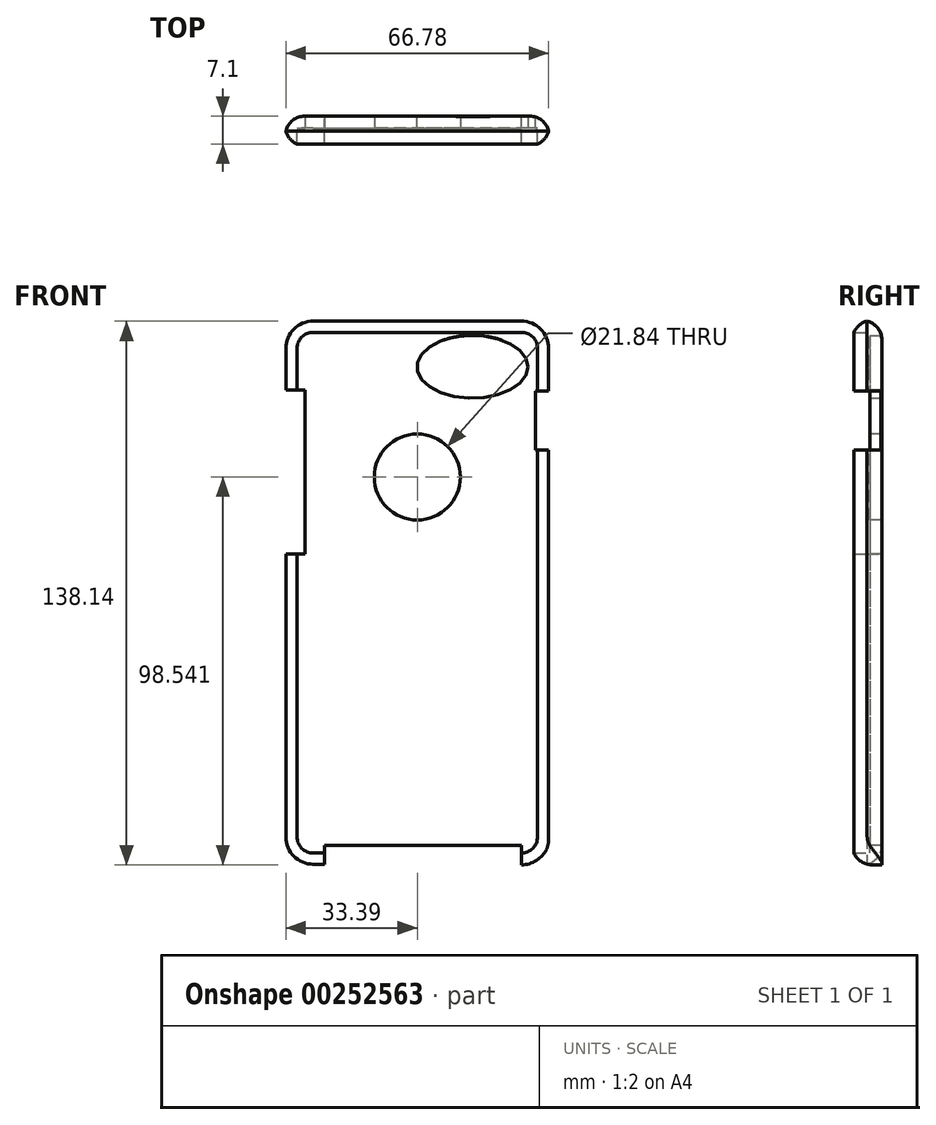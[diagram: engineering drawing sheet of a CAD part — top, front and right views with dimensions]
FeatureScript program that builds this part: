
annotation { "Feature Type Name" : "Feature", "Feature Type Description" : "" }
export const myFeature = defineFeature(function(context is Context, id is Id, definition is map)
    precondition{}
    {
        {
            var Q0;
            Q0=qCreatedBy(makeId("Front.planeOp"),FACE);
            var sketch = newSketch(context, id + "F0", { "sketchPlane" : qUnion([Q0])});
            skLineSegment(sketch, "E0.bottom", {"start": v(-33.55, 69.15) * mm, "end": v(33.55, 69.15) * mm});
            skLineSegment(sketch, "E0.top", {"start": v(-33.55, -69.15) * mm, "end": v(33.55, -69.15) * mm});
            skLineSegment(sketch, "E0.left", {"start": v(-33.55, 69.15) * mm, "end": v(-33.55, -69.15) * mm});
            skLineSegment(sketch, "E0.right", {"start": v(33.55, 69.15) * mm, "end": v(33.55, -69.15) * mm});
            skPoint(sketch, "E0.middle", {"position": v(0, 0) * mm});
            skSolve(sketch);
        }
        {
            var Q0;
            Q0=makeQuery(id+"F0.imprint","IMPRINT",FACE,{"disambiguationData":[TD([[makeQuery(id+"F0.imprint","IMPRINT",EDGE,{"derivedFrom":sQuery(id+"F0.wireOp",EDGE,"E0.bottom")}),-1.0]])]});
            extrude(context, id + "F1", {"entities" : qUnion([Q0]), "depth" : 7.1 * mm});
        }
        {
            var Q0;
            Q0=makeQuery(id+"F1.opExtrude","SWEPT_EDGE",EDGE,{"disambiguationData":[OSD([sQuery(id+"F0.wireOp",EDGE,"E0.bottom"),sQuery(id+"F0.wireOp",EDGE,"E0.right")])]});
            var Q1;
            Q1=makeQuery(id+"F1.opExtrude","SWEPT_EDGE",EDGE,{"disambiguationData":[OSD([sQuery(id+"F0.wireOp",EDGE,"E0.top"),sQuery(id+"F0.wireOp",EDGE,"E0.left")])]});
            var Q2;
            Q2=makeQuery(id+"F1.opExtrude","SWEPT_EDGE",EDGE,{"disambiguationData":[OSD([sQuery(id+"F0.wireOp",EDGE,"E0.top"),sQuery(id+"F0.wireOp",EDGE,"E0.right")])]});
            var Q3;
            Q3=makeQuery(id+"F1.opExtrude","SWEPT_EDGE",EDGE,{"disambiguationData":[OSD([sQuery(id+"F0.wireOp",EDGE,"E0.bottom"),sQuery(id+"F0.wireOp",EDGE,"E0.left")])]});
            fillet(context, id + "F2", {"entities" : qUnion([Q0, Q1, Q2, Q3]), "radius" : 7.1 * mm, "tangentPropagation" : true, "allowEdgeOverflow" : false});
        }
        {
            var Q0;
            Q0=makeQuery(id+"F1.opExtrude","CAP_FACE",FACE,{"disambiguationData":[OSD([sQuery(id+"F0.wireOp",EDGE,"E0.bottom"),sQuery(id+"F0.wireOp",EDGE,"E0.top"),sQuery(id+"F0.wireOp",EDGE,"E0.left"),sQuery(id+"F0.wireOp",EDGE,"E0.right")])],"isStart":false});
            shell(context, id + "F3", {"entities" : qUnion([Q0]), "thickness" : 3 * mm});
        }
        {
            var Q0;
            Q0=makeQuery(id+"F3.opShell","OFFSET_FACE",FACE,{"disambiguationData":[OSD([sQuery(id+"F0.wireOp",EDGE,"E0.bottom"),sQuery(id+"F0.wireOp",EDGE,"E0.top"),sQuery(id+"F0.wireOp",EDGE,"E0.left"),sQuery(id+"F0.wireOp",EDGE,"E0.right")])]});
            var sketch = newSketch(context, id + "F4", { "sketchPlane" : qUnion([Q0])});
            skEllipse(sketch, "E1", {"center": v(14.06, 57.39) * mm, "majorRadius": 14.1 * mm, "minorRadius": 7.98 * mm, "majorAxis": v(1, 0)});
            skCircle(sketch, "E2", {"center": v(0, 29.4) * mm, "radius": 10.92 * mm});
            skSolve(sketch);
        }
        {
            var Q0;
            Q0=makeQuery(id+"F4.imprint","IMPRINT",FACE,{"disambiguationData":[TD([[makeQuery(id+"F4.imprint","IMPRINT",EDGE,{"derivedFrom":sQuery(id+"F4.wireOp",EDGE,"E1")}),1.0]])]});
            var Q1;
            Q1=makeQuery(id+"F4.imprint","IMPRINT",FACE,{"disambiguationData":[TD([[makeQuery(id+"F4.imprint","IMPRINT",EDGE,{"derivedFrom":sQuery(id+"F4.wireOp",EDGE,"E2")}),1.0]])]});
            extrude(context, id + "F5", {"entities" : qUnion([Q0, Q1]), "operationType" : NewBodyOperationType.REMOVE, "endBound" : BoundingType.SYMMETRIC, "oppositeDirection" : true, "depth" : 25 * mm});
        }
        {
            var Q0;
            Q0=makeQuery(id+"F1.opExtrude","SWEPT_FACE",FACE,{"disambiguationData":[OSD([sQuery(id+"F0.wireOp",EDGE,"E0.top")])]});
            var sketch = newSketch(context, id + "F6", { "sketchPlane" : qUnion([Q0])});
            skLineSegment(sketch, "E3.bottom", {"start": v(-23.53, 0) * mm, "end": v(26.45, 0) * mm});
            skLineSegment(sketch, "E3.top", {"start": v(-23.53, 7.1) * mm, "end": v(26.45, 7.1) * mm});
            skLineSegment(sketch, "E3.left", {"start": v(-23.53, 0) * mm, "end": v(-23.53, 7.1) * mm});
            skLineSegment(sketch, "E3.right", {"start": v(26.45, 0) * mm, "end": v(26.45, 7.1) * mm});
            skLineSegment(sketch, "E4.bottom", {"start": v(-23.53, 7.1) * mm, "end": v(-26.45, 7.1) * mm});
            skLineSegment(sketch, "E4.top", {"start": v(-23.53, 7.1) * mm, "end": v(-26.45, 7.1) * mm});
            skLineSegment(sketch, "E4.left", {"start": v(-23.53, 7.1) * mm, "end": v(-23.53, 7.1) * mm});
            skLineSegment(sketch, "E4.right", {"start": v(-26.45, 7.1) * mm, "end": v(-26.45, 7.1) * mm});
            skSolve(sketch);
        }
        {
            var Q0;
            Q0=makeQuery(id+"F6.imprint","IMPRINT",FACE,{"disambiguationData":[TD([[makeQuery(id+"F6.imprint","IMPRINT",EDGE,{"derivedFrom":sQuery(id+"F6.wireOp",EDGE,"E3.bottom")}),1.0]])]});
            extrude(context, id + "F7", {"entities" : qUnion([Q0]), "operationType" : NewBodyOperationType.REMOVE, "endBound" : BoundingType.SYMMETRIC, "oppositeDirection" : true, "depth" : 10 * mm});
        }
        {
            var Q0;
            Q0=makeQuery(id+"F1.opExtrude","SWEPT_FACE",FACE,{"disambiguationData":[OSD([sQuery(id+"F0.wireOp",EDGE,"E0.left")])]});
            var sketch = newSketch(context, id + "F8", { "sketchPlane" : qUnion([Q0])});
            skLineSegment(sketch, "E5.bottom", {"start": v(0, 51.55) * mm, "end": v(7.1, 51.55) * mm});
            skLineSegment(sketch, "E5.top", {"start": v(0, 9.8) * mm, "end": v(7.1, 9.8) * mm});
            skLineSegment(sketch, "E5.left", {"start": v(0, 51.55) * mm, "end": v(0, 9.8) * mm});
            skLineSegment(sketch, "E5.right", {"start": v(7.1, 51.55) * mm, "end": v(7.1, 9.8) * mm});
            skSolve(sketch);
        }
        {
            var Q0;
            Q0=makeQuery(id+"F8.imprint","IMPRINT",FACE,{"disambiguationData":[TD([[makeQuery(id+"F8.imprint","IMPRINT",EDGE,{"derivedFrom":sQuery(id+"F8.wireOp",EDGE,"E5.bottom")}),-1.0]])]});
            extrude(context, id + "F9", {"entities" : qUnion([Q0]), "operationType" : NewBodyOperationType.REMOVE, "endBound" : BoundingType.SYMMETRIC, "oppositeDirection" : true, "depth" : 10 * mm});
        }
        {
            var Q0;
            Q0=makeQuery(id+"F1.opExtrude","SWEPT_FACE",FACE,{"disambiguationData":[OSD([sQuery(id+"F0.wireOp",EDGE,"E0.right")])]});
            var sketch = newSketch(context, id + "F10", { "sketchPlane" : qUnion([Q0])});
            skLineSegment(sketch, "E6.bottom", {"start": v(-7.1, 51.21) * mm, "end": v(0, 51.21) * mm});
            skLineSegment(sketch, "E6.top", {"start": v(-7.1, 36.21) * mm, "end": v(0, 36.21) * mm});
            skLineSegment(sketch, "E6.left", {"start": v(-7.1, 51.21) * mm, "end": v(-7.1, 36.21) * mm});
            skLineSegment(sketch, "E6.right", {"start": v(0, 51.21) * mm, "end": v(0, 36.21) * mm});
            skSolve(sketch);
        }
        {
            var Q0;
            Q0=makeQuery(id+"F10.imprint","IMPRINT",FACE,{"disambiguationData":[TD([[makeQuery(id+"F10.imprint","IMPRINT",EDGE,{"derivedFrom":sQuery(id+"F10.wireOp",EDGE,"E6.bottom")}),-1.0]])]});
            extrude(context, id + "F11", {"entities" : qUnion([Q0]), "operationType" : NewBodyOperationType.REMOVE, "endBound" : BoundingType.SYMMETRIC, "oppositeDirection" : true, "depth" : 7 * mm});
        }
        {
            var Q0;
            {var subQ0=sQuery(id+"F0.wireOp",EDGE,"E0.left");var subQ1=sQuery(id+"F0.wireOp",EDGE,"E0.bottom");Q0=makeQuery(id+"F2.opFillet","BLEND_EDGE",EDGE,{"blendedFrom":[makeQuery(id+"F1.opExtrude","SWEPT_EDGE",EDGE,{"disambiguationData":[OSD([subQ1,subQ0])]}),makeQuery(id+"F1.opExtrude","CAP_FACE",FACE,{"disambiguationData":[OSD([subQ1,sQuery(id+"F0.wireOp",EDGE,"E0.top"),subQ0,sQuery(id+"F0.wireOp",EDGE,"E0.right")])],"isStart":false})],"blendedInto":[makeQuery(id+"F1.opExtrude","CAP_FACE",FACE,{"disambiguationData":[OSD([subQ1,sQuery(id+"F0.wireOp",EDGE,"E0.top"),subQ0,sQuery(id+"F0.wireOp",EDGE,"E0.right")])],"isStart":false})]});}
            var Q1;
            {var subQ0=sQuery(id+"F0.wireOp",EDGE,"E0.left");Q1=makeQuery(id+"F9.boolean.opBoolean","SPLIT",EDGE,{"disambiguationData":[TD([makeQuery(id+"F9.opExtrude","SWEPT_FACE",FACE,{"disambiguationData":[OSD([sQuery(id+"F8.wireOp",EDGE,"E5.bottom")])]})])],"derivedFrom":makeQuery(id+"F1.opExtrude","CAP_EDGE",EDGE,{"disambiguationData":[OSD([subQ0])],"isStart":true})});}
            var Q2;
            Q2=makeQuery(id+"F9.boolean.opBoolean","COPY",EDGE,{"derivedFrom":makeQuery(id+"F9.opExtrude","CAP_EDGE",EDGE,{"disambiguationData":[OSD([sQuery(id+"F8.wireOp",EDGE,"E5.left")])],"isStart":false})});
            var Q3;
            {var subQ0=sQuery(id+"F0.wireOp",EDGE,"E0.left");Q3=makeQuery(id+"F9.boolean.opBoolean","SPLIT",EDGE,{"disambiguationData":[TD([makeQuery(id+"F9.opExtrude","SWEPT_FACE",FACE,{"disambiguationData":[OSD([sQuery(id+"F8.wireOp",EDGE,"E5.top")])]})])],"derivedFrom":makeQuery(id+"F1.opExtrude","CAP_EDGE",EDGE,{"disambiguationData":[OSD([subQ0])],"isStart":true})});}
            var Q4;
            {var subQ0=sQuery(id+"F0.wireOp",EDGE,"E0.left");Q4=makeQuery(id+"F9.boolean.opBoolean","SPLIT",EDGE,{"disambiguationData":[TD([makeQuery(id+"F9.opExtrude","SWEPT_FACE",FACE,{"disambiguationData":[OSD([sQuery(id+"F8.wireOp",EDGE,"E5.top")])]})])],"derivedFrom":makeQuery(id+"F1.opExtrude","CAP_EDGE",EDGE,{"disambiguationData":[OSD([subQ0])],"isStart":false})});}
            var Q5;
            {var subQ0=sQuery(id+"F0.wireOp",EDGE,"E0.right");var subQ1=sQuery(id+"F0.wireOp",EDGE,"E0.top");Q5=makeQuery(id+"F2.opFillet","BLEND_EDGE",EDGE,{"blendedFrom":[makeQuery(id+"F1.opExtrude","SWEPT_EDGE",EDGE,{"disambiguationData":[OSD([subQ1,subQ0])]}),makeQuery(id+"F1.opExtrude","CAP_FACE",FACE,{"disambiguationData":[OSD([sQuery(id+"F0.wireOp",EDGE,"E0.bottom"),subQ1,sQuery(id+"F0.wireOp",EDGE,"E0.left"),subQ0])],"isStart":false})],"blendedInto":[makeQuery(id+"F1.opExtrude","CAP_FACE",FACE,{"disambiguationData":[OSD([sQuery(id+"F0.wireOp",EDGE,"E0.bottom"),subQ1,sQuery(id+"F0.wireOp",EDGE,"E0.left"),subQ0])],"isStart":false})]});}
            fillet(context, id + "F12", {"entities" : qUnion([Q0, Q1, Q2, Q3, Q4, Q5]), "radius" : 5 * mm, "tangentPropagation" : true, "allowEdgeOverflow" : false});
        }
    });
